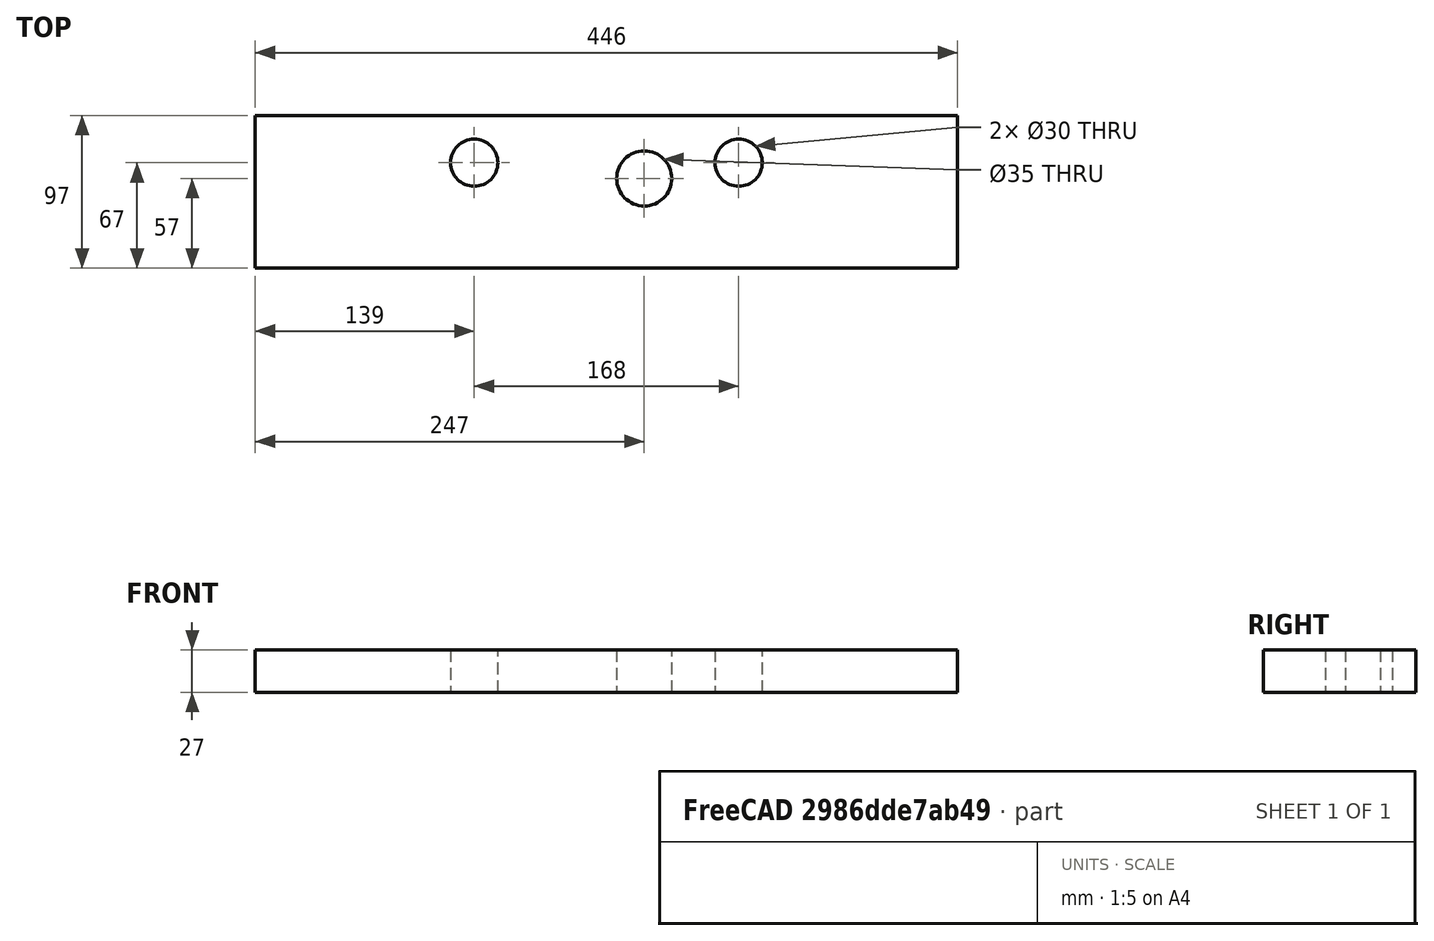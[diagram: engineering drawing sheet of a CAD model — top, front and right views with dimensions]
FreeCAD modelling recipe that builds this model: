
FCSTD DOCUMENT  (FreeCAD 0.20R25131 (Git))
Label: Innen_vorne
License: All rights reserved
LicenseURL: http://en.wikipedia.org/wiki/All_rights_reserved
objects: Part::FeaturePython×9, Part::Cylinder×3, App::FeaturePython×2, Part::Box×1, Part::MultiFuse×1, Part::Cut×1
note: 14 computed .brp shape members not serialized (recipe doc carries the construction recipe); baked Part::Feature solids carry a one-line shape summary decoded from their .brp
EXTERNAL_REF file=Grunddaten.FCStd obj=Spreadsheet

FEATURE [Part::Box] Box  label="Cube"
  AttacherType = Attacher::AttachEngine3D
  Height = 27
  Length = 446
  Placement = pos=(-223,0,0) rot=(0,0,1;0rad)
  Width = 97
  expr: .Placement.Base.x = -Length / 2
  expr: Height = <<Grunddaten>>#Spreadsheet.Plattendicke
  expr: Width = <<Grunddaten>>#Spreadsheet.Hoehe
  expr: Length = <<Grunddaten>>#Spreadsheet.Innenmass
FEATURE [Part::Cylinder] Cylinder  label="Führung_rechts"
  Angle = 360
  AttacherType = Attacher::AttachEngine3D
  FirstAngle = 0
  Height = 30
  Placement = pos=(84,67,0) rot=(0,0,1;0rad)
  Radius = 15
  SecondAngle = 0
  expr: .Placement.Base.x = Grunddaten#Spreadsheet.Spindel_Links
  expr: .Placement.Base.y = Grunddaten#Spreadsheet.Hoehe - Grunddaten#Spreadsheet.Spindel_Hoehe
FEATURE [Part::Cylinder] Cylinder001  label="Führung_links"
  Angle = 360
  AttacherType = Attacher::AttachEngine3D
  FirstAngle = 0
  Height = 30
  Placement = pos=(-84,67,0) rot=(0,0,1;0rad)
  Radius = 15
  SecondAngle = 0
  expr: .Placement.Base.x = -Grunddaten#Spreadsheet.Spindel_Links
  expr: .Placement.Base.y = Grunddaten#Spreadsheet.Hoehe - Grunddaten#Spreadsheet.Spindel_Hoehe
FEATURE [Part::Cylinder] Cylinder002  label="Spindel"
  Angle = 360
  AttacherType = Attacher::AttachEngine3D
  FirstAngle = 0
  Height = 30
  Placement = pos=(24,57,0) rot=(0,0,1;0rad)
  Radius = 17.5
  SecondAngle = 0
  expr: .Placement.Base.y = Grunddaten#Spreadsheet.Hoehe - Grunddaten#Spreadsheet.Spindel_Antrieb_Hoehe
  expr: .Placement.Base.x = Grunddaten#Spreadsheet.Spindel_Antrieb
FEATURE [App::FeaturePython] Constraints  # WARN: FeaturePython — macro-defined, semantics opaque (R4)
  _Version = 1
FEATURE [Part::MultiFuse] Fusion
  Shapes = -> [Cylinder,Cylinder001,Cylinder002]
FEATURE [Part::Cut] Cut
  Base = -> Box
  Tool = -> Fusion
FEATURE [Part::FeaturePython] Parts  # WARN: FeaturePython — macro-defined, semantics opaque (R4)
  Group = -> [Box,Cylinder,Cylinder001,Cylinder002,Fusion,Cut]
  GroupMode = 0
FEATURE [Part::FeaturePython] Assembly  label="Innen_vorne"  # WARN: FeaturePython — macro-defined, semantics opaque (R4)
  AutoRelax = true
  BuildShape = 0
  Freeze = false
  Group = -> [Constraints,Elements,Parts]
  Verbose = false
  _SolverType = 1
  _Version = 1
FEATURE [App::FeaturePython] Elements  # WARN: FeaturePython — macro-defined, semantics opaque (R4)
  Group = -> [Element,Element001,Element002,Element003,Element004,Element005,Element006]
FEATURE [Part::FeaturePython] Element  label="Vorne"  # link proxy (typed FeaturePython)
  Detach = false
  LinkTransform = true
  LinkedObject = -> Cut [Face3]
  _Parent = -> Elements
FEATURE [Part::FeaturePython] Element001  label="Oben"  # link proxy (typed FeaturePython)
  Detach = false
  LinkTransform = true
  LinkedObject = -> Cut [Face4]
  _Parent = -> Elements
FEATURE [Part::FeaturePython] Element002  label="Spindel"  # link proxy (typed FeaturePython)
  Detach = false
  LinkTransform = true
  LinkedObject = -> Cut [Face7]
  _Parent = -> Elements
FEATURE [Part::FeaturePython] Element003  # link proxy (typed FeaturePython)
  Detach = false
  LinkTransform = true
  LinkedObject = -> Cut [Edge10]
  _Parent = -> Elements
FEATURE [Part::FeaturePython] Element004  # link proxy (typed FeaturePython)
  Detach = false
  LinkTransform = true
  LinkedObject = -> Cut [Face1]
  _Parent = -> Elements
FEATURE [Part::FeaturePython] Element005  # link proxy (typed FeaturePython)
  Detach = false
  LinkTransform = true
  LinkedObject = -> Cut [Face6]
  _Parent = -> Elements
FEATURE [Part::FeaturePython] Element006  # link proxy (typed FeaturePython)
  Detach = false
  LinkTransform = true
  LinkedObject = -> Cut [Face2]
  _Parent = -> Elements
